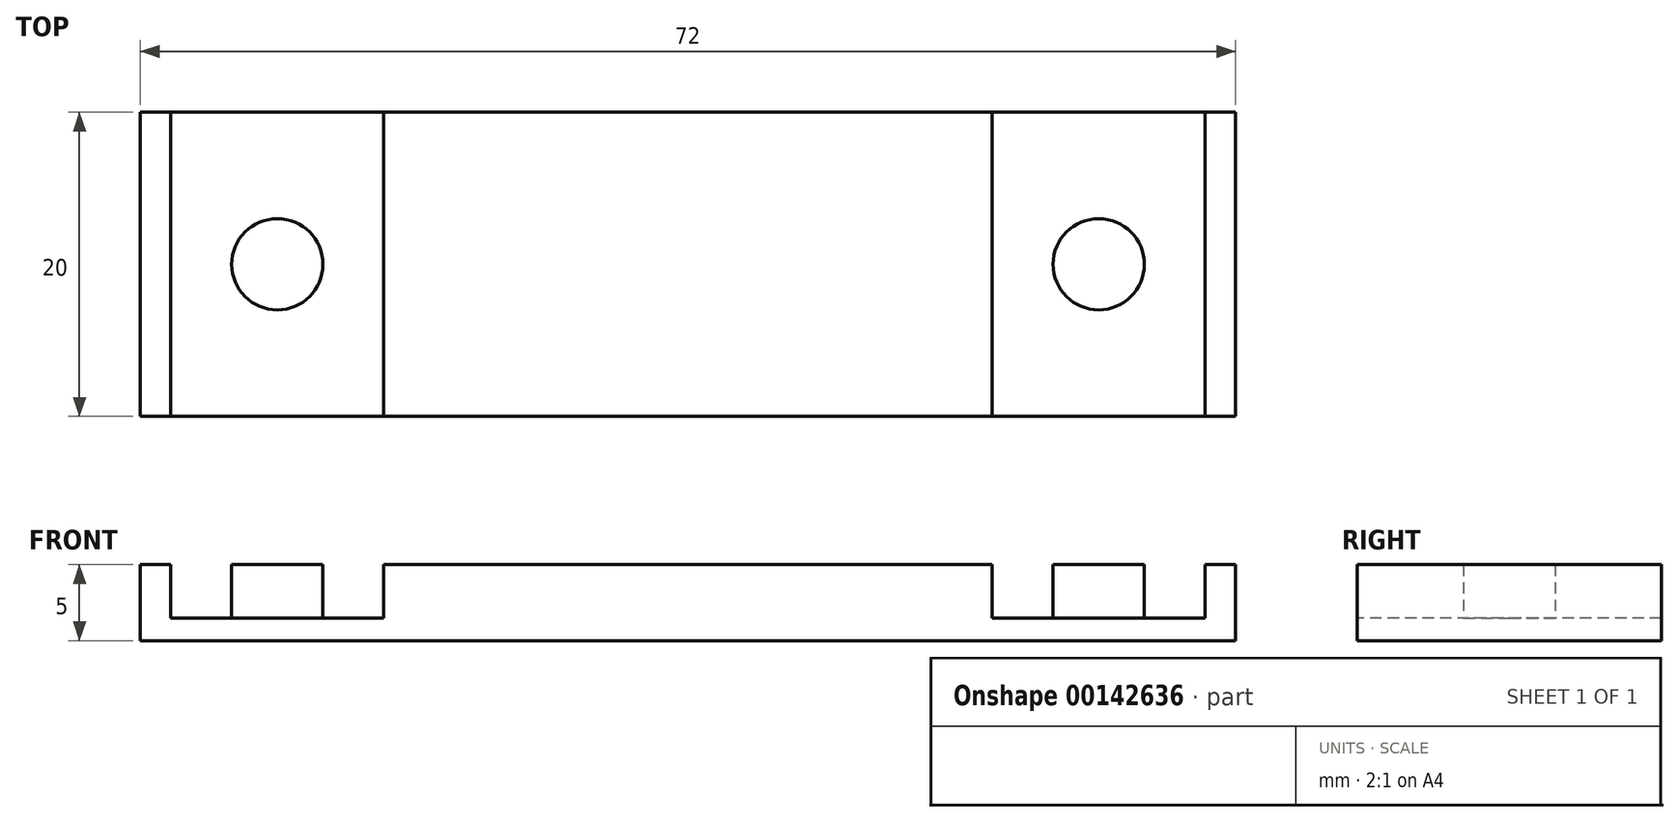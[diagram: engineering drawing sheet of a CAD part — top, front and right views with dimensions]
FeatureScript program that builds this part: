
annotation { "Feature Type Name" : "Feature", "Feature Type Description" : "" }
export const myFeature = defineFeature(function(context is Context, id is Id, definition is map)
    precondition{}
    {
        {
            var Q0;
            Q0=qCreatedBy(makeId("Top.planeOp"),FACE);
            var sketch = newSketch(context, id + "F0", { "sketchPlane" : qUnion([Q0])});
            skLineSegment(sketch, "E0.bottom", {"start": v(36, 10) * mm, "end": v(-36, 10) * mm});
            skLineSegment(sketch, "E0.top", {"start": v(36, -10) * mm, "end": v(-36, -10) * mm});
            skLineSegment(sketch, "E0.left", {"start": v(36, 10) * mm, "end": v(36, -10) * mm});
            skLineSegment(sketch, "E0.right", {"start": v(-36, 10) * mm, "end": v(-36, -10) * mm});
            skPoint(sketch, "E0.middle", {"position": v(0, 0) * mm});
            skSolve(sketch);
        }
        {
            var Q0;
            Q0 = qSketchRegion(id + "F0", true);
            extrude(context, id + "F1", {"entities" : qUnion([Q0]), "depth" : 5 * mm});
        }
        {
            var Q0;
            Q0=makeQuery(id+"F1.opExtrude","CAP_FACE",FACE,{"disambiguationData":[OSD([sQuery(id+"F0.wireOp",EDGE,"E0.bottom"),sQuery(id+"F0.wireOp",EDGE,"E0.top"),sQuery(id+"F0.wireOp",EDGE,"E0.left"),sQuery(id+"F0.wireOp",EDGE,"E0.right")])],"isStart":false});
            var sketch = newSketch(context, id + "F2", { "sketchPlane" : qUnion([Q0])});
            skLineSegment(sketch, "E1.bottom", {"start": v(20, 10) * mm, "end": v(34, 10) * mm});
            skLineSegment(sketch, "E1.top", {"start": v(20, -10) * mm, "end": v(34, -10) * mm});
            skLineSegment(sketch, "E1.left", {"start": v(20, 10) * mm, "end": v(20, -10) * mm});
            skLineSegment(sketch, "E1.right", {"start": v(34, 10) * mm, "end": v(34, -10) * mm});
            skLineSegment(sketch, "E2.bottom", {"start": v(-34, 10) * mm, "end": v(-20, 10) * mm});
            skLineSegment(sketch, "E2.top", {"start": v(-34, -10) * mm, "end": v(-20, -10) * mm});
            skLineSegment(sketch, "E2.left", {"start": v(-34, 10) * mm, "end": v(-34, -10) * mm});
            skLineSegment(sketch, "E2.right", {"start": v(-20, 10) * mm, "end": v(-20, -10) * mm});
            skSolve(sketch);
        }
        {
            var Q0;
            Q0 = qSketchRegion(id + "F2", true);
            extrude(context, id + "F3", {"entities" : qUnion([Q0]), "operationType" : NewBodyOperationType.REMOVE, "oppositeDirection" : true, "depth" : 3.5 * mm});
        }
        {
            var Q0;
            Q0=makeQuery(id+"F3.boolean.opBoolean","COPY",FACE,{"derivedFrom":makeQuery(id+"F3.opExtrude","CAP_FACE",FACE,{"disambiguationData":[OSD([sQuery(id+"F2.wireOp",EDGE,"E2.bottom"),sQuery(id+"F2.wireOp",EDGE,"E2.top"),sQuery(id+"F2.wireOp",EDGE,"E2.left"),sQuery(id+"F2.wireOp",EDGE,"E2.right")])],"isStart":false})});
            var sketch = newSketch(context, id + "F4", { "sketchPlane" : qUnion([Q0])});
            skLineSegment(sketch, "E3", {"start": v(-34, 10) * mm, "end": v(-20, -10) * mm, "construction": true});
            skLineSegment(sketch, "E4", {"start": v(34, -10) * mm, "end": v(20, 10) * mm, "construction": true});
            skCircle(sketch, "E5", {"center": v(-27, 0) * mm, "radius": 3 * mm});
            skPoint(sketch, "E5.perimeterSnap0", {"position": v(-27, 0) * mm});
            skCircle(sketch, "E6", {"center": v(27, 0) * mm, "radius": 3 * mm});
            skSolve(sketch);
        }
        {
            var Q0;
            Q0 = qSketchRegion(id + "F4", true);
            extrude(context, id + "F5", {"entities" : qUnion([Q0]), "operationType" : NewBodyOperationType.ADD, "depth" : 3.5 * mm});
        }
    });
